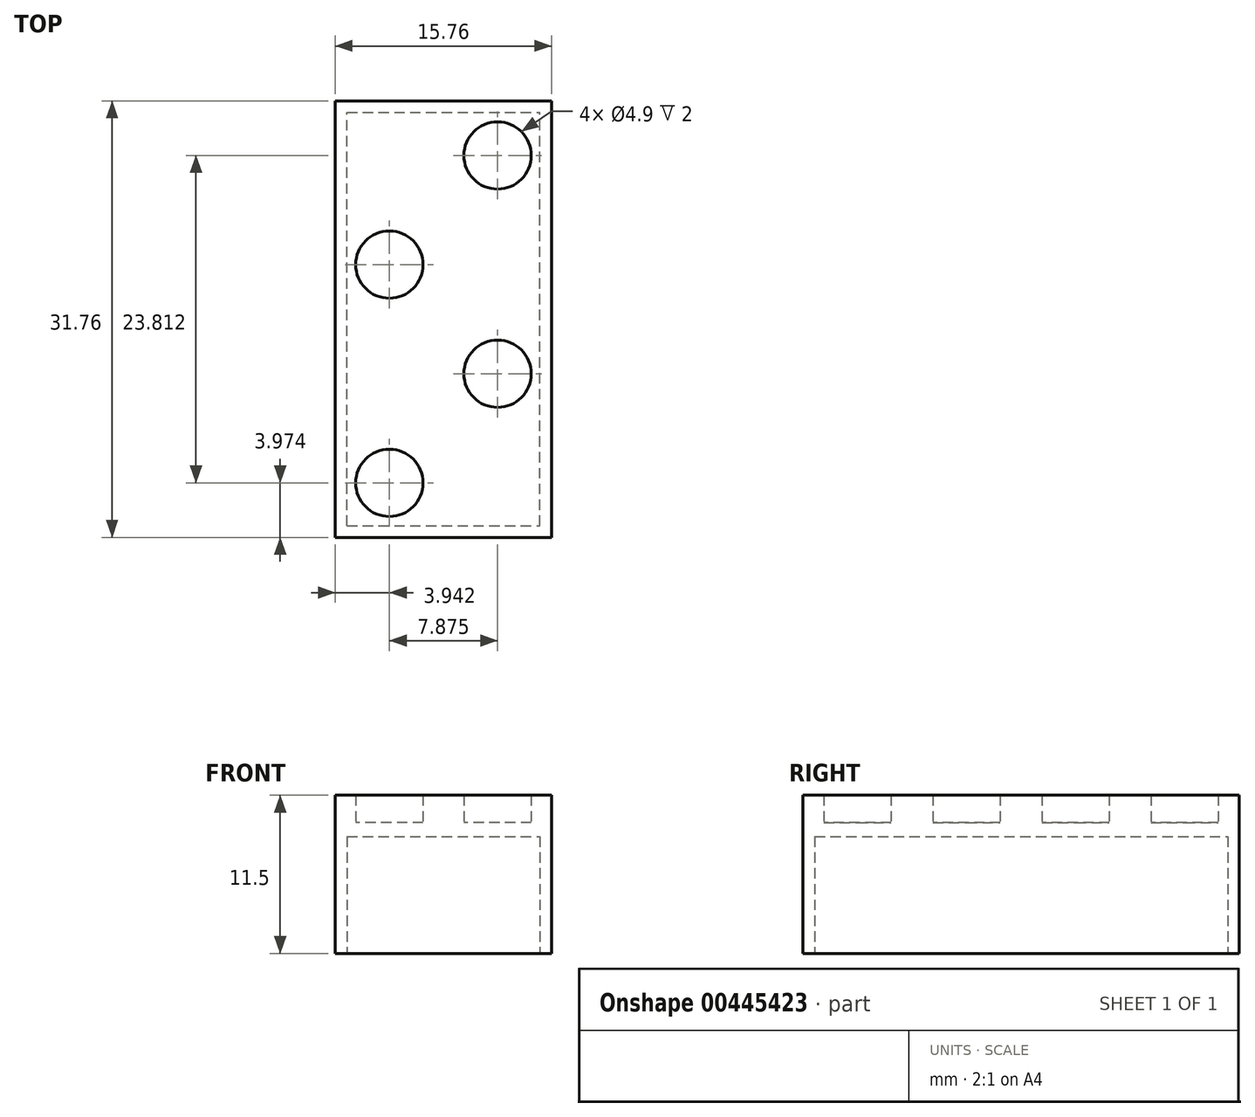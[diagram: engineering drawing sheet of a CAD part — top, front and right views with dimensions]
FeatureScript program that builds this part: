
annotation { "Feature Type Name" : "Feature", "Feature Type Description" : "" }
export const myFeature = defineFeature(function(context is Context, id is Id, definition is map)
    precondition{}
    {
        {
            var Q0;
            Q0=qCreatedBy(makeId("Front.planeOp"),FACE);
            var sketch = newSketch(context, id + "F0", { "sketchPlane" : qUnion([Q0])});
            skLineSegment(sketch, "E0.bottom", {"start": v(7.88, 4.75) * mm, "end": v(-7.87, 4.75) * mm});
            skLineSegment(sketch, "E0.top", {"start": v(7.87, -4.75) * mm, "end": v(-7.88, -4.75) * mm});
            skLineSegment(sketch, "E0.left", {"start": v(7.88, 4.75) * mm, "end": v(7.87, -4.75) * mm});
            skLineSegment(sketch, "E0.right", {"start": v(-7.87, 4.75) * mm, "end": v(-7.88, -4.75) * mm});
            skPoint(sketch, "E0.middle", {"position": v(0, 0) * mm});
            skSolve(sketch);
        }
        {
            var Q0;
            Q0=makeQuery(id+"F0.imprint","IMPRINT",FACE,{"disambiguationData":[TD([[makeQuery(id+"F0.imprint","IMPRINT",EDGE,{"derivedFrom":sQuery(id+"F0.wireOp",EDGE,"E0.bottom")}),1.0]])]});
            extrude(context, id + "F1", {"entities" : qUnion([Q0]), "endBound" : BoundingType.SYMMETRIC, "depth" : 31.75 * mm});
        }
        {
            var Q0;
            Q0=makeQuery(id+"F1.opExtrude","SWEPT_FACE",FACE,{"disambiguationData":[OSD([sQuery(id+"F0.wireOp",EDGE,"E0.bottom")])]});
            var sketch = newSketch(context, id + "F2", { "sketchPlane" : qUnion([Q0])});
            skLineSegment(sketch, "E1", {"start": v(7.88, 0) * mm, "end": v(7.88, -15.88) * mm});
            skLineSegment(sketch, "E2", {"start": v(7.88, -15.88) * mm, "end": v(-7.87, -15.88) * mm});
            skLineSegment(sketch, "E3", {"start": v(-7.87, -15.88) * mm, "end": v(-7.87, 0) * mm});
            skLineSegment(sketch, "E4", {"start": v(-7.87, 15.88) * mm, "end": v(7.88, 15.88) * mm});
            skLineSegment(sketch, "E5", {"start": v(7.88, 15.88) * mm, "end": v(7.88, 0) * mm});
            skLineSegment(sketch, "E6", {"start": v(-7.87, 15.88) * mm, "end": v(-7.87, 0) * mm});
            skLineSegment(sketch, "E7", {"start": v(-7.87, 15.88) * mm, "end": v(0, 15.88) * mm});
            skCircle(sketch, "E8", {"center": v(-3.94, 11.9) * mm, "radius": 2.45 * mm});
            skCircle(sketch, "E9.MirrorC", {"center": v(3.94, 11.9) * mm, "radius": 2.45 * mm});
            skCircle(sketch, "E10.MirrorC", {"center": v(-3.94, 3.97) * mm, "radius": 2.45 * mm});
            skCircle(sketch, "E11.MirrorC", {"center": v(3.94, 3.97) * mm, "radius": 2.45 * mm});
            skCircle(sketch, "E12.MirrorC", {"center": v(3.94, -3.97) * mm, "radius": 2.45 * mm});
            skCircle(sketch, "E13.MirrorC", {"center": v(3.94, -11.9) * mm, "radius": 2.45 * mm});
            skCircle(sketch, "E14.MirrorC", {"center": v(-3.94, -11.9) * mm, "radius": 2.45 * mm});
            skCircle(sketch, "E15.MirrorC", {"center": v(-3.94, -3.97) * mm, "radius": 2.45 * mm});
            skSolve(sketch);
        }
        {
            var Q0;
            Q0=makeQuery(id+"F2.imprint","IMPRINT",FACE,{"disambiguationData":[TD([[makeQuery(id+"F2.imprint","IMPRINT",EDGE,{"derivedFrom":sQuery(id+"F2.wireOp",EDGE,"E8")}),1.0]])]});
            var Q1;
            Q1=makeQuery(id+"F2.imprint","IMPRINT",FACE,{"disambiguationData":[TD([[makeQuery(id+"F2.imprint","IMPRINT",EDGE,{"derivedFrom":sQuery(id+"F2.wireOp",EDGE,"E9.MirrorC")}),-1.0]])]});
            var Q2;
            Q2=makeQuery(id+"F2.imprint","IMPRINT",FACE,{"disambiguationData":[TD([[makeQuery(id+"F2.imprint","IMPRINT",EDGE,{"derivedFrom":sQuery(id+"F2.wireOp",EDGE,"E11.MirrorC")}),1.0]])]});
            var Q3;
            Q3=makeQuery(id+"F2.imprint","IMPRINT",FACE,{"disambiguationData":[TD([[makeQuery(id+"F2.imprint","IMPRINT",EDGE,{"derivedFrom":sQuery(id+"F2.wireOp",EDGE,"E10.MirrorC")}),-1.0]])]});
            var Q4;
            Q4=makeQuery(id+"F2.imprint","IMPRINT",FACE,{"disambiguationData":[TD([[makeQuery(id+"F2.imprint","IMPRINT",EDGE,{"derivedFrom":sQuery(id+"F2.wireOp",EDGE,"E15.MirrorC")}),1.0]])]});
            var Q5;
            Q5=makeQuery(id+"F2.imprint","IMPRINT",FACE,{"disambiguationData":[TD([[makeQuery(id+"F2.imprint","IMPRINT",EDGE,{"derivedFrom":sQuery(id+"F2.wireOp",EDGE,"E12.MirrorC")}),-1.0]])]});
            var Q6;
            Q6=makeQuery(id+"F2.imprint","IMPRINT",FACE,{"disambiguationData":[TD([[makeQuery(id+"F2.imprint","IMPRINT",EDGE,{"derivedFrom":sQuery(id+"F2.wireOp",EDGE,"E14.MirrorC")}),-1.0]])]});
            var Q7;
            Q7=makeQuery(id+"F2.imprint","IMPRINT",FACE,{"disambiguationData":[TD([[makeQuery(id+"F2.imprint","IMPRINT",EDGE,{"derivedFrom":sQuery(id+"F2.wireOp",EDGE,"E13.MirrorC")}),1.0]])]});
            extrude(context, id + "F3", {"entities" : qUnion([Q0, Q1, Q2, Q3, Q4, Q5, Q6, Q7]), "operationType" : NewBodyOperationType.ADD, "depth" : 2 * mm});
        }
        {
            var Q0;
            Q0=makeQuery(id+"F1.opExtrude","SWEPT_FACE",FACE,{"disambiguationData":[OSD([sQuery(id+"F0.wireOp",EDGE,"E0.top")])]});
            var sketch = newSketch(context, id + "F4", { "sketchPlane" : qUnion([Q0])});
            skLineSegment(sketch, "E16.bottom", {"start": v(-7.03, 15.03) * mm, "end": v(7.03, 15.03) * mm});
            skLineSegment(sketch, "E16.top", {"start": v(-7.03, -15.03) * mm, "end": v(7.03, -15.03) * mm});
            skLineSegment(sketch, "E16.left", {"start": v(-7.03, 15.03) * mm, "end": v(-7.03, -15.03) * mm});
            skLineSegment(sketch, "E16.right", {"start": v(7.03, 15.03) * mm, "end": v(7.03, -15.03) * mm});
            skPoint(sketch, "E16.middle", {"position": v(0, 0) * mm});
            skSolve(sketch);
        }
        {
            var Q0;
            Q0=makeQuery(id+"F4.imprint","IMPRINT",FACE,{"disambiguationData":[TD([[makeQuery(id+"F4.imprint","IMPRINT",EDGE,{"derivedFrom":sQuery(id+"F4.wireOp",EDGE,"E16.bottom")}),-1.0]])]});
            extrude(context, id + "F5", {"entities" : qUnion([Q0]), "operationType" : NewBodyOperationType.REMOVE, "oppositeDirection" : true, "depth" : 8.5 * mm});
        }
    });
